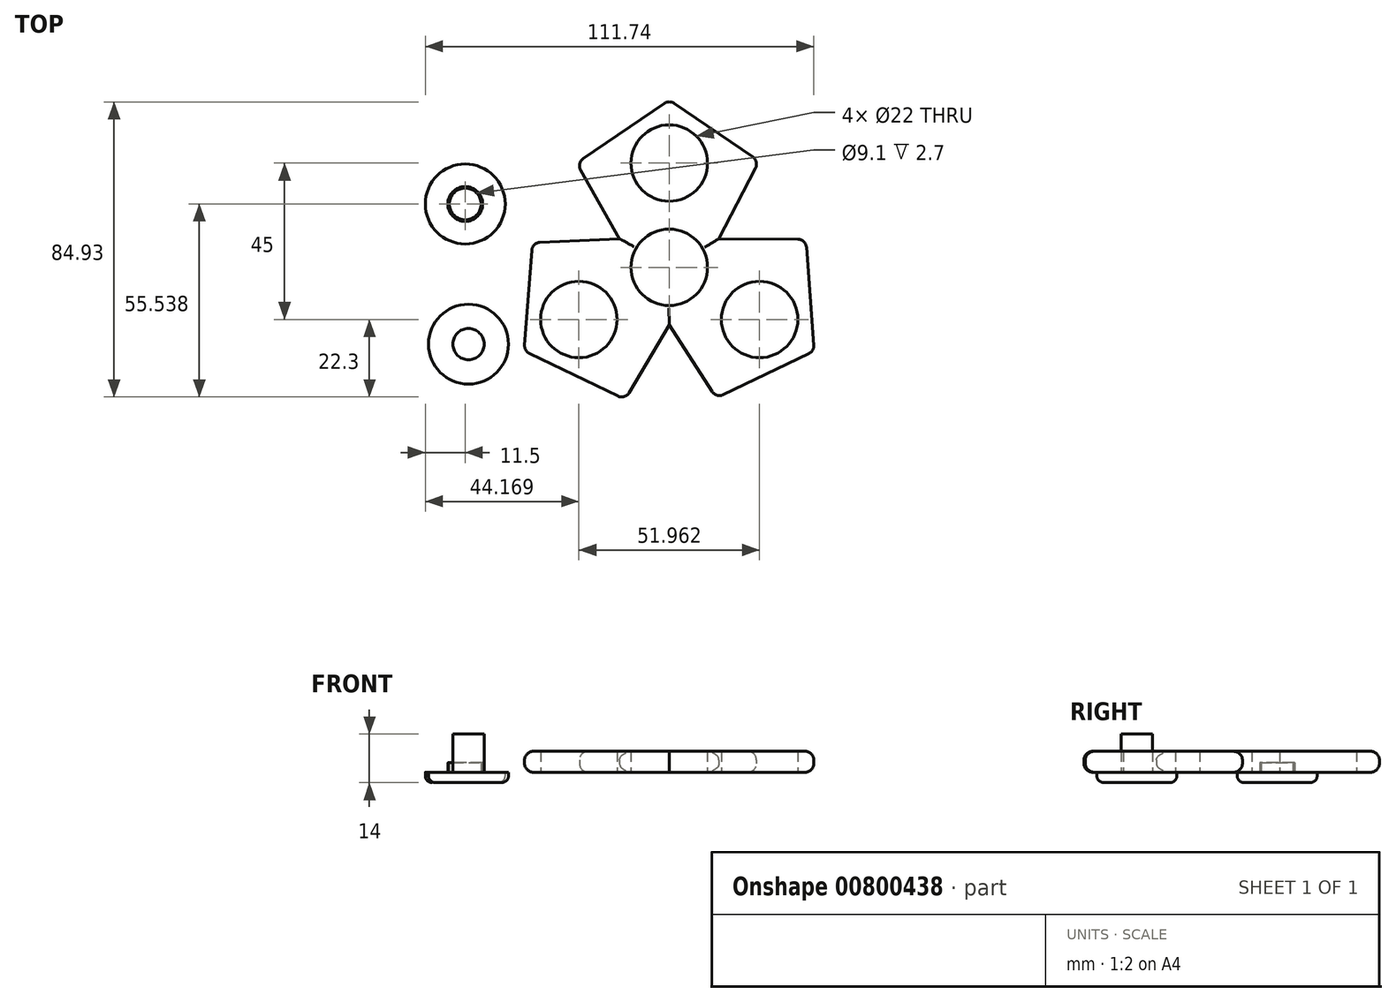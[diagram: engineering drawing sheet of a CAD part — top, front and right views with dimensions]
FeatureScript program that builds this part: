
annotation { "Feature Type Name" : "Feature", "Feature Type Description" : "" }
export const myFeature = defineFeature(function(context is Context, id is Id, definition is map)
    precondition{}
    {
        {
            var Q0;
            Q0=qCreatedBy(makeId("Top.planeOp"),FACE);
            var sketch = newSketch(context, id + "F0", { "sketchPlane" : qUnion([Q0])});
            skCircle(sketch, "E0", {"center": v(0, 0) * mm, "radius": 11 * mm});
            skCircle(sketch, "E1", {"center": v(0, 30) * mm, "radius": 11 * mm});
            skLineSegment(sketch, "E2", {"start": v(0, 48.16) * mm, "end": v(25.82, 30.54) * mm});
            skLineSegment(sketch, "E3", {"start": v(25.82, 30.54) * mm, "end": v(14.29, 8.25) * mm});
            skLineSegment(sketch, "E4", {"start": v(0, 48.16) * mm, "end": v(-26.61, 30) * mm});
            skLineSegment(sketch, "E5", {"start": v(-26.61, 30) * mm, "end": v(-14.29, 8.25) * mm});
            skLineSegment(sketch, "E6.1.0", {"start": v(-41.7, -24.08) * mm, "end": v(-39.36, 7.1) * mm});
            skCircle(sketch, "E6.1.1", {"center": v(-25.98, -15) * mm, "radius": 11 * mm});
            skLineSegment(sketch, "E6.1.2", {"start": v(-39.36, 7.1) * mm, "end": v(-14.29, 8.25) * mm});
            skLineSegment(sketch, "E6.1.3", {"start": v(-12.67, -38.05) * mm, "end": v(0, -16.5) * mm});
            skLineSegment(sketch, "E6.1.4", {"start": v(-41.7, -24.08) * mm, "end": v(-12.67, -38.05) * mm});
            skLineSegment(sketch, "E6.2.0", {"start": v(41.7, -24.08) * mm, "end": v(13.54, -37.63) * mm});
            skCircle(sketch, "E6.2.1", {"center": v(25.98, -15) * mm, "radius": 11 * mm});
            skLineSegment(sketch, "E6.2.2", {"start": v(13.54, -37.63) * mm, "end": v(0, -16.5) * mm});
            skLineSegment(sketch, "E6.2.3", {"start": v(39.29, 8.05) * mm, "end": v(14.29, 8.25) * mm});
            skLineSegment(sketch, "E6.2.4", {"start": v(41.7, -24.08) * mm, "end": v(39.29, 8.05) * mm});
            skSolve(sketch);
        }
        {
            var Q0;
            Q0 = qSketchRegion(id + "F0", true);
            extrude(context, id + "F1", {"entities" : qUnion([Q0]), "depth" : 6 * mm, "offsetDistance" : 25 * mm});
        }
        {
            var Q0;
            Q0=makeQuery(id+"F1.opExtrude","CAP_EDGE",EDGE,{"disambiguationData":[OSD([sQuery(id+"F0.wireOp",EDGE,"E4")])],"isStart":true});
            var Q1;
            Q1=makeQuery(id+"F1.opExtrude","CAP_EDGE",EDGE,{"disambiguationData":[OSD([sQuery(id+"F0.wireOp",EDGE,"E4")])],"isStart":false});
            var Q2;
            Q2=makeQuery(id+"F1.opExtrude","CAP_EDGE",EDGE,{"disambiguationData":[OSD([sQuery(id+"F0.wireOp",EDGE,"E5")])],"isStart":true});
            var Q3;
            Q3=makeQuery(id+"F1.opExtrude","CAP_EDGE",EDGE,{"disambiguationData":[OSD([sQuery(id+"F0.wireOp",EDGE,"E5")])],"isStart":false});
            var Q4;
            Q4=makeQuery(id+"F1.opExtrude","CAP_EDGE",EDGE,{"disambiguationData":[OSD([sQuery(id+"F0.wireOp",EDGE,"E6.1.2")])],"isStart":true});
            var Q5;
            Q5=makeQuery(id+"F1.opExtrude","CAP_EDGE",EDGE,{"disambiguationData":[OSD([sQuery(id+"F0.wireOp",EDGE,"E6.1.2")])],"isStart":false});
            var Q6;
            Q6=makeQuery(id+"F1.opExtrude","CAP_EDGE",EDGE,{"disambiguationData":[OSD([sQuery(id+"F0.wireOp",EDGE,"E6.1.0")])],"isStart":true});
            var Q7;
            Q7=makeQuery(id+"F1.opExtrude","CAP_EDGE",EDGE,{"disambiguationData":[OSD([sQuery(id+"F0.wireOp",EDGE,"E6.1.0")])],"isStart":false});
            var Q8;
            Q8=makeQuery(id+"F1.opExtrude","CAP_EDGE",EDGE,{"disambiguationData":[OSD([sQuery(id+"F0.wireOp",EDGE,"E6.1.4")])],"isStart":true});
            var Q9;
            Q9=makeQuery(id+"F1.opExtrude","CAP_EDGE",EDGE,{"disambiguationData":[OSD([sQuery(id+"F0.wireOp",EDGE,"E6.1.4")])],"isStart":false});
            var Q10;
            Q10=makeQuery(id+"F1.opExtrude","CAP_EDGE",EDGE,{"disambiguationData":[OSD([sQuery(id+"F0.wireOp",EDGE,"E6.1.3")])],"isStart":true});
            var Q11;
            Q11=makeQuery(id+"F1.opExtrude","CAP_EDGE",EDGE,{"disambiguationData":[OSD([sQuery(id+"F0.wireOp",EDGE,"E6.1.3")])],"isStart":false});
            var Q12;
            Q12=makeQuery(id+"F1.opExtrude","CAP_EDGE",EDGE,{"disambiguationData":[OSD([sQuery(id+"F0.wireOp",EDGE,"E6.2.2")])],"isStart":false});
            var Q13;
            Q13=makeQuery(id+"F1.opExtrude","CAP_EDGE",EDGE,{"disambiguationData":[OSD([sQuery(id+"F0.wireOp",EDGE,"E6.2.2")])],"isStart":true});
            var Q14;
            Q14=makeQuery(id+"F1.opExtrude","CAP_EDGE",EDGE,{"disambiguationData":[OSD([sQuery(id+"F0.wireOp",EDGE,"E6.2.0")])],"isStart":true});
            var Q15;
            Q15=makeQuery(id+"F1.opExtrude","CAP_EDGE",EDGE,{"disambiguationData":[OSD([sQuery(id+"F0.wireOp",EDGE,"E6.2.0")])],"isStart":false});
            var Q16;
            Q16=makeQuery(id+"F1.opExtrude","CAP_EDGE",EDGE,{"disambiguationData":[OSD([sQuery(id+"F0.wireOp",EDGE,"E6.2.4")])],"isStart":true});
            var Q17;
            Q17=makeQuery(id+"F1.opExtrude","CAP_EDGE",EDGE,{"disambiguationData":[OSD([sQuery(id+"F0.wireOp",EDGE,"E6.2.4")])],"isStart":false});
            var Q18;
            Q18=makeQuery(id+"F1.opExtrude","CAP_EDGE",EDGE,{"disambiguationData":[OSD([sQuery(id+"F0.wireOp",EDGE,"E6.2.3")])],"isStart":false});
            var Q19;
            Q19=makeQuery(id+"F1.opExtrude","CAP_EDGE",EDGE,{"disambiguationData":[OSD([sQuery(id+"F0.wireOp",EDGE,"E3")])],"isStart":false});
            var Q20;
            Q20=makeQuery(id+"F1.opExtrude","CAP_EDGE",EDGE,{"disambiguationData":[OSD([sQuery(id+"F0.wireOp",EDGE,"E6.2.3")])],"isStart":true});
            var Q21;
            Q21=makeQuery(id+"F1.opExtrude","CAP_EDGE",EDGE,{"disambiguationData":[OSD([sQuery(id+"F0.wireOp",EDGE,"E3")])],"isStart":true});
            var Q22;
            Q22=makeQuery(id+"F1.opExtrude","CAP_EDGE",EDGE,{"disambiguationData":[OSD([sQuery(id+"F0.wireOp",EDGE,"E2")])],"isStart":false});
            var Q23;
            Q23=makeQuery(id+"F1.opExtrude","CAP_EDGE",EDGE,{"disambiguationData":[OSD([sQuery(id+"F0.wireOp",EDGE,"E2")])],"isStart":true});
            var Q24;
            Q24=makeQuery(id+"F1.opExtrude","SWEPT_EDGE",EDGE,{"disambiguationData":[OSD([sQuery(id+"F0.wireOp",EDGE,"E6.1.0"),sQuery(id+"F0.wireOp",EDGE,"E6.1.2")])]});
            var Q25;
            Q25=makeQuery(id+"F1.opExtrude","SWEPT_EDGE",EDGE,{"disambiguationData":[OSD([sQuery(id+"F0.wireOp",EDGE,"E4"),sQuery(id+"F0.wireOp",EDGE,"E5")])]});
            var Q26;
            Q26=makeQuery(id+"F1.opExtrude","SWEPT_EDGE",EDGE,{"disambiguationData":[OSD([sQuery(id+"F0.wireOp",EDGE,"E2"),sQuery(id+"F0.wireOp",EDGE,"E4")])]});
            var Q27;
            Q27=makeQuery(id+"F1.opExtrude","SWEPT_EDGE",EDGE,{"disambiguationData":[OSD([sQuery(id+"F0.wireOp",EDGE,"E2"),sQuery(id+"F0.wireOp",EDGE,"E3")])]});
            var Q28;
            Q28=makeQuery(id+"F1.opExtrude","SWEPT_EDGE",EDGE,{"disambiguationData":[OSD([sQuery(id+"F0.wireOp",EDGE,"E6.2.3"),sQuery(id+"F0.wireOp",EDGE,"E6.2.4")])]});
            var Q29;
            Q29=makeQuery(id+"F1.opExtrude","SWEPT_EDGE",EDGE,{"disambiguationData":[OSD([sQuery(id+"F0.wireOp",EDGE,"E6.2.0"),sQuery(id+"F0.wireOp",EDGE,"E6.2.4")])]});
            var Q30;
            Q30=makeQuery(id+"F1.opExtrude","SWEPT_EDGE",EDGE,{"disambiguationData":[OSD([sQuery(id+"F0.wireOp",EDGE,"E6.2.0"),sQuery(id+"F0.wireOp",EDGE,"E6.2.2")])]});
            var Q31;
            Q31=makeQuery(id+"F1.opExtrude","SWEPT_EDGE",EDGE,{"disambiguationData":[OSD([sQuery(id+"F0.wireOp",EDGE,"E6.1.3"),sQuery(id+"F0.wireOp",EDGE,"E6.1.4")])]});
            var Q32;
            Q32=makeQuery(id+"F1.opExtrude","SWEPT_EDGE",EDGE,{"disambiguationData":[OSD([sQuery(id+"F0.wireOp",EDGE,"E6.1.0"),sQuery(id+"F0.wireOp",EDGE,"E6.1.4")])]});
            fillet(context, id + "F2", {"entities" : qUnion([Q0, Q1, Q2, Q3, Q4, Q5, Q6, Q7, Q8, Q9, Q10, Q11, Q12, Q13, Q14, Q15, Q16, Q17, Q18, Q19, Q20, Q21, Q22, Q23, Q24, Q25, Q26, Q27, Q28, Q29, Q30, Q31, Q32]), "radius" : 2.5 * mm, "tangentPropagation" : true, "allowEdgeOverflow" : false});
        }
        {
            var Q0;
            Q0=qCreatedBy(makeId("Top.planeOp"),FACE);
            var sketch = newSketch(context, id + "F3", { "sketchPlane" : qUnion([Q0])});
            skCircle(sketch, "E7", {"center": v(-56.01, 44.8) * mm, "radius": 4.5 * mm});
            skCircle(sketch, "E8", {"center": v(-56.01, 44.8) * mm, "radius": 11.5 * mm});
            skSolve(sketch);
        }
        {
            var Q0;
            Q0=sQuery(id+"F3.wireOp",EDGE,"E7");
            extrude(context, id + "F4", {"bodyType" : ToolBodyType.SURFACE, "surfaceEntities" : qUnion([Q0]), "depth" : 11 * mm, "offsetDistance" : 25 * mm});
        }
        {
            var Q0;
            Q0=sQuery(id+"F3.wireOp",EDGE,"E8");
            extrude(context, id + "F5", {"bodyType" : ToolBodyType.SURFACE, "surfaceEntities" : qUnion([Q0]), "oppositeDirection" : true, "depth" : 3 * mm, "offsetDistance" : 25 * mm});
        }
        {
            var Q0;
            Q0=makeQuery(id+"F3.imprint","IMPRINT",FACE,{"disambiguationData":[TD([[makeQuery(id+"F3.imprint","IMPRINT",EDGE,{"derivedFrom":sQuery(id+"F3.wireOp",EDGE,"E7")}),-1.0]])]});
            extrude(context, id + "F6", {"entities" : qUnion([Q0]), "oppositeDirection" : true, "depth" : 3 * mm, "offsetDistance" : 25 * mm});
        }
        {
            var Q0;
            Q0=makeQuery(id+"F3.imprint","IMPRINT",FACE,{"disambiguationData":[TD([[makeQuery(id+"F3.imprint","IMPRINT",EDGE,{"derivedFrom":sQuery(id+"F3.wireOp",EDGE,"E7")}),1.0]])]});
            extrude(context, id + "F7", {"entities" : qUnion([Q0]), "depth" : 11 * mm, "offsetDistance" : 25 * mm});
        }
        {
            var Q0;
            Q0=makeQuery(id+"F3.imprint","IMPRINT",FACE,{"disambiguationData":[TD([[makeQuery(id+"F3.imprint","IMPRINT",EDGE,{"derivedFrom":sQuery(id+"F3.wireOp",EDGE,"E7")}),1.0]])]});
            extrude(context, id + "F8", {"entities" : qUnion([Q0]), "oppositeDirection" : true, "depth" : 3 * mm, "offsetDistance" : 25 * mm});
        }
        {
            var Q0;
            Q0=qCreatedBy(makeId("Top.planeOp"),FACE);
            var sketch = newSketch(context, id + "F9", { "sketchPlane" : qUnion([Q0])});
            skCircle(sketch, "E9", {"center": v(-57.44, 13.6) * mm, "radius": 4.55 * mm});
            skCircle(sketch, "E10", {"center": v(-57.44, 13.6) * mm, "radius": 11.5 * mm});
            skCircle(sketch, "E11", {"center": v(-57.44, 13.6) * mm, "radius": 5 * mm});
            skSolve(sketch);
        }
        {
            var Q0;
            Q0=makeQuery(id+"F9.imprint","IMPRINT",FACE,{"disambiguationData":[TD([[makeQuery(id+"F9.imprint","IMPRINT",EDGE,{"derivedFrom":sQuery(id+"F9.wireOp",EDGE,"E9")}),-1.0]])]});
            extrude(context, id + "F10", {"entities" : qUnion([Q0]), "depth" : 3 * mm, "offsetDistance" : 25 * mm});
        }
        {
            var Q0;
            Q0=makeQuery(id+"F9.imprint","IMPRINT",FACE,{"disambiguationData":[TD([[makeQuery(id+"F9.imprint","IMPRINT",EDGE,{"derivedFrom":sQuery(id+"F9.wireOp",EDGE,"E10")}),1.0]])]});
            extrude(context, id + "F11", {"entities" : qUnion([Q0]), "oppositeDirection" : true, "depth" : 3 * mm, "offsetDistance" : 25 * mm});
        }
        {
            var Q0;
            Q0=makeQuery(id+"F9.imprint","IMPRINT",FACE,{"disambiguationData":[TD([[makeQuery(id+"F9.imprint","IMPRINT",EDGE,{"derivedFrom":sQuery(id+"F9.wireOp",EDGE,"E9")}),1.0]])]});
            extrude(context, id + "F12", {"entities" : qUnion([Q0]), "operationType" : NewBodyOperationType.ADD, "oppositeDirection" : true, "depth" : 3 * mm, "offsetDistance" : 25 * mm});
        }
        {
            var Q0;
            Q0=makeQuery(id+"F6.opExtrude","SWEPT_BODY",BODY,{"disambiguationData":[OSD([sQuery(id+"F3.wireOp",EDGE,"E7"),sQuery(id+"F3.wireOp",EDGE,"E8")])]});
            var Q1;
            Q1=makeQuery(id+"F7.opExtrude","SWEPT_BODY",BODY,{"disambiguationData":[OSD([sQuery(id+"F3.wireOp",EDGE,"E7")])]});
            var Q2;
            Q2=makeQuery(id+"F8.opExtrude","SWEPT_BODY",BODY,{"disambiguationData":[OSD([sQuery(id+"F3.wireOp",EDGE,"E7")])]});
            var Q3;
            Q3=makeQuery(id+"F5.opExtrude","SWEPT_BODY",BODY,{"disambiguationData":[OSD([sQuery(id+"F3.wireOp",EDGE,"E8")])]});
            var Q4;
            Q4=makeQuery(id+"F4.opExtrude","SWEPT_BODY",BODY,{"disambiguationData":[OSD([sQuery(id+"F3.wireOp",EDGE,"E7")])]});
            deleteBodies(context, id + "F13", {"entities" : qUnion([Q0, Q1, Q2, Q3, Q4])});
        }
        {
            var Q0;
            Q0=qCreatedBy(makeId("Top.planeOp"),FACE);
            var sketch = newSketch(context, id + "F14", { "sketchPlane" : qUnion([Q0])});
            skCircle(sketch, "E12", {"center": v(-57.72, -22.1) * mm, "radius": 4.5 * mm});
            skCircle(sketch, "E13", {"center": v(-57.72, -22.1) * mm, "radius": 11.5 * mm});
            skSolve(sketch);
        }
        {
            var Q0;
            Q0=makeQuery(id+"F14.imprint","IMPRINT",FACE,{"disambiguationData":[TD([[makeQuery(id+"F14.imprint","IMPRINT",EDGE,{"derivedFrom":sQuery(id+"F14.wireOp",EDGE,"E12")}),1.0]])]});
            var Q1;
            Q1=makeQuery(id+"F14.imprint","IMPRINT",FACE,{"disambiguationData":[TD([[makeQuery(id+"F14.imprint","IMPRINT",EDGE,{"derivedFrom":sQuery(id+"F14.wireOp",EDGE,"E12")}),-1.0]])]});
            extrude(context, id + "F15", {"entities" : qUnion([Q0, Q1]), "oppositeDirection" : true, "depth" : 3 * mm, "offsetDistance" : 25 * mm});
        }
        {
            var Q0;
            Q0=makeQuery(id+"F14.imprint","IMPRINT",FACE,{"disambiguationData":[TD([[makeQuery(id+"F14.imprint","IMPRINT",EDGE,{"derivedFrom":sQuery(id+"F14.wireOp",EDGE,"E12")}),1.0]])]});
            extrude(context, id + "F16", {"entities" : qUnion([Q0]), "operationType" : NewBodyOperationType.ADD, "depth" : 11 * mm, "offsetDistance" : 25 * mm});
        }
        {
            var Q0;
            Q0=makeQuery(id+"F15.opExtrude","CAP_EDGE",EDGE,{"disambiguationData":[OSD([sQuery(id+"F14.wireOp",EDGE,"E13")])],"isStart":false});
            fillet(context, id + "F17", {"entities" : qUnion([Q0]), "radius" : 2 * mm, "tangentPropagation" : true, "allowEdgeOverflow" : false});
        }
        {
            var Q0;
            Q0=makeQuery(id+"F11.opExtrude","SWEPT_BODY",BODY,{"disambiguationData":[OSD([sQuery(id+"F9.wireOp",EDGE,"E10"),sQuery(id+"F9.wireOp",EDGE,"E11")])]});
            var Q1;
            Q1=makeQuery(id+"F10.opExtrude","SWEPT_BODY",BODY,{"disambiguationData":[OSD([sQuery(id+"F9.wireOp",EDGE,"E9"),sQuery(id+"F9.wireOp",EDGE,"E11")])]});
            var Q2;
            Q2=makeQuery(id+"F12.opExtrude","SWEPT_BODY",BODY,{"disambiguationData":[OSD([sQuery(id+"F9.wireOp",EDGE,"E9")])]});
            deleteBodies(context, id + "F18", {"entities" : qUnion([Q0, Q1, Q2])});
        }
        {
            var Q0;
            Q0=qCreatedBy(makeId("Top.planeOp"),FACE);
            var sketch = newSketch(context, id + "F19", { "sketchPlane" : qUnion([Q0])});
            skCircle(sketch, "E14", {"center": v(-58.65, 18.24) * mm, "radius": 4.55 * mm});
            skCircle(sketch, "E15", {"center": v(-58.65, 18.24) * mm, "radius": 5 * mm});
            skCircle(sketch, "E16", {"center": v(-58.65, 18.24) * mm, "radius": 11.5 * mm});
            skSolve(sketch);
        }
        {
            var Q0;
            Q0=makeQuery(id+"F19.imprint","IMPRINT",FACE,{"disambiguationData":[TD([[makeQuery(id+"F19.imprint","IMPRINT",EDGE,{"derivedFrom":sQuery(id+"F19.wireOp",EDGE,"E15")}),-1.0]])]});
            var Q1;
            Q1=makeQuery(id+"F19.imprint","IMPRINT",FACE,{"disambiguationData":[TD([[makeQuery(id+"F19.imprint","IMPRINT",EDGE,{"derivedFrom":sQuery(id+"F19.wireOp",EDGE,"E14")}),1.0]])]});
            var Q2;
            Q2=makeQuery(id+"F19.imprint","IMPRINT",FACE,{"disambiguationData":[TD([[makeQuery(id+"F19.imprint","IMPRINT",EDGE,{"derivedFrom":sQuery(id+"F19.wireOp",EDGE,"E14")}),-1.0]])]});
            extrude(context, id + "F20", {"entities" : qUnion([Q0, Q1, Q2]), "oppositeDirection" : true, "depth" : 3 * mm, "offsetDistance" : 25 * mm});
        }
        {
            var Q0;
            Q0=makeQuery(id+"F19.imprint","IMPRINT",FACE,{"disambiguationData":[TD([[makeQuery(id+"F19.imprint","IMPRINT",EDGE,{"derivedFrom":sQuery(id+"F19.wireOp",EDGE,"E14")}),-1.0]])]});
            extrude(context, id + "F21", {"entities" : qUnion([Q0]), "operationType" : NewBodyOperationType.ADD, "depth" : 2.7 * mm, "offsetDistance" : 25 * mm});
        }
        {
            var Q0;
            Q0=makeQuery(id+"F20.opExtrude","CAP_EDGE",EDGE,{"disambiguationData":[OSD([sQuery(id+"F19.wireOp",EDGE,"E16")])],"isStart":false});
            fillet(context, id + "F22", {"entities" : qUnion([Q0]), "radius" : 2 * mm, "tangentPropagation" : true, "allowEdgeOverflow" : false});
        }
    });
